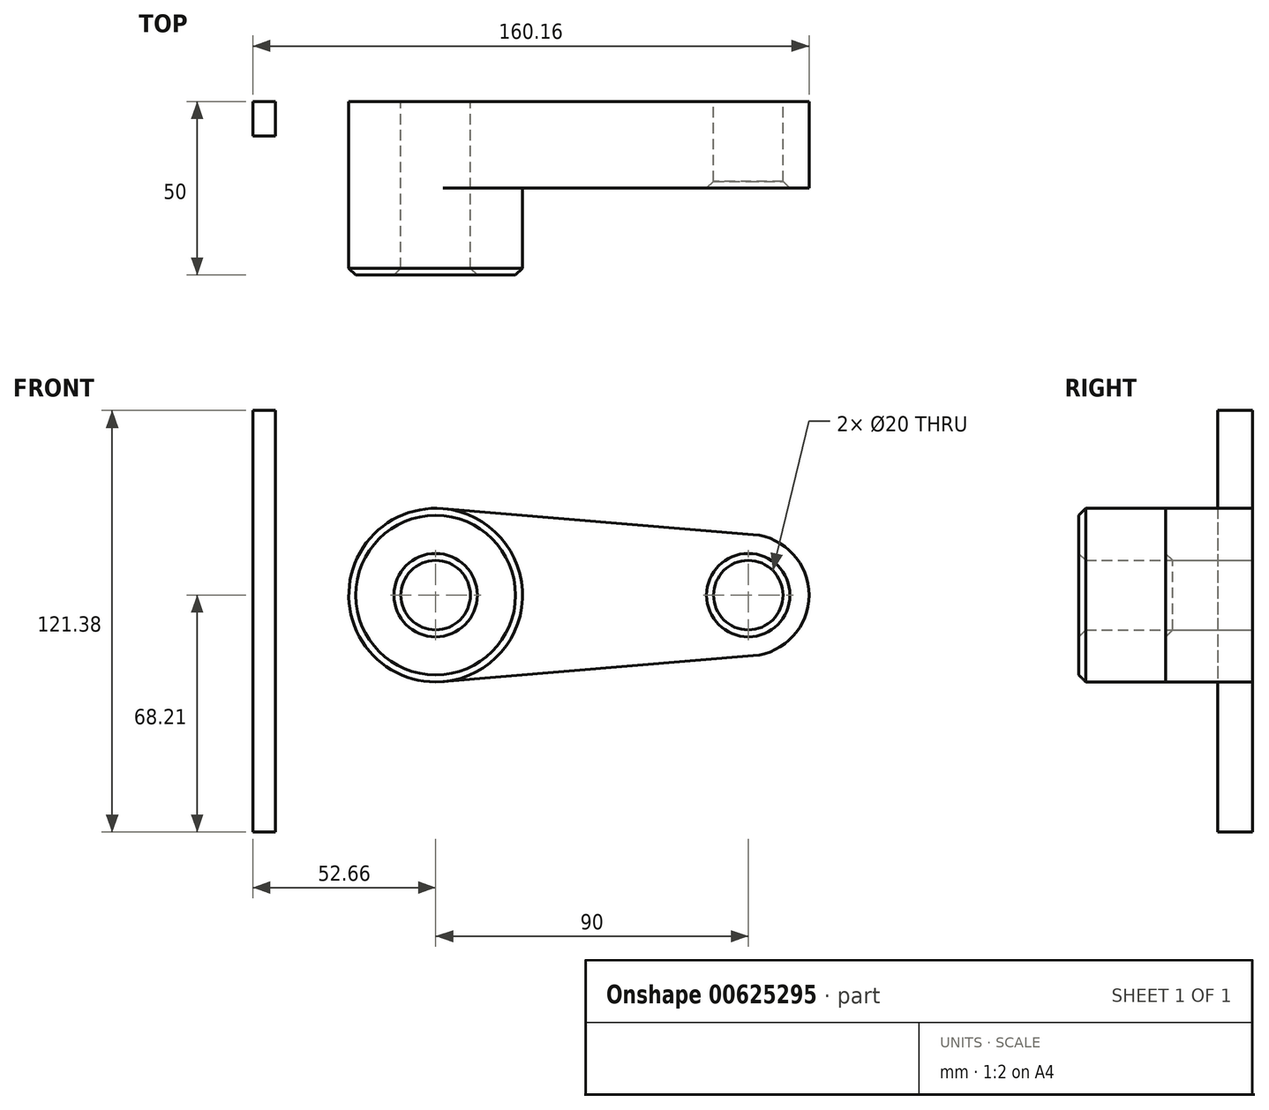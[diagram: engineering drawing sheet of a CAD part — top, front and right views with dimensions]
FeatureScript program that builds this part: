
annotation { "Feature Type Name" : "Feature", "Feature Type Description" : "" }
export const myFeature = defineFeature(function(context is Context, id is Id, definition is map)
    precondition{}
    {
        {
            var Q0;
            Q0=qCreatedBy(makeId("Front.planeOp"),FACE);
            var sketch = newSketch(context, id + "F0", { "sketchPlane" : qUnion([Q0])});
            skCircle(sketch, "E0", {"center": v(0, 0) * mm, "radius": 25 * mm});
            skCircle(sketch, "E1", {"center": v(90, 0) * mm, "radius": 17.5 * mm});
            skLineSegment(sketch, "E2", {"start": v(2.08, 24.91) * mm, "end": v(91.46, 17.44) * mm});
            skLineSegment(sketch, "E3", {"start": v(2.08, -24.91) * mm, "end": v(91.46, -17.44) * mm});
            skCircle(sketch, "E4", {"center": v(0, 0) * mm, "radius": 10 * mm});
            skCircle(sketch, "E5", {"center": v(90, 0) * mm, "radius": 10 * mm});
            skSolve(sketch);
        }
        {
            var Q0;
            Q0=qSketchRegion(id+"F0",true);
            extrude(context, id + "F1", {"entities" : qUnion([Q0]), "depth" : 25 * mm});
        }
        {
            var Q0;
            Q0=makeQuery(id+"F0.imprint","IMPRINT",FACE,{"disambiguationData":[TD([[makeQuery(id+"F0.imprint","IMPRINT",EDGE,{"derivedFrom":sQuery(id+"F0.wireOp",EDGE,"E4")}),-1.0]])]});
            extrude(context, id + "F2", {"entities" : qUnion([Q0]), "operationType" : NewBodyOperationType.ADD, "depth" : 50 * mm});
        }
        {
            var Q0;
            Q0=makeQuery(id+"F2.opExtrude","CAP_EDGE",EDGE,{"disambiguationData":[OSD([sQuery(id+"F0.wireOp",EDGE,"E0")])],"isStart":false});
            var Q1;
            Q1=makeQuery(id+"F2.opExtrude","CAP_EDGE",EDGE,{"disambiguationData":[OSD([sQuery(id+"F0.wireOp",EDGE,"E4")])],"isStart":false});
            var Q2;
            Q2=makeQuery(id+"F1.opExtrude","CAP_EDGE",EDGE,{"disambiguationData":[OSD([sQuery(id+"F0.wireOp",EDGE,"E5")])],"isStart":false});
            chamfer(context, id + "F3", {"entities" : qUnion([Q0, Q1, Q2]), "width" : 2 * mm, "tangentPropagation" : true});
        }
        {
            var Q0;
            Q0=qCreatedBy(makeId("Front.planeOp"),FACE);
            var sketch = newSketch(context, id + "F4", { "sketchPlane" : qUnion([Q0])});
            skLineSegment(sketch, "E6.bottom", {"start": v(-52.66, 53.17) * mm, "end": v(-46.1, 53.17) * mm});
            skLineSegment(sketch, "E6.top", {"start": v(-52.66, -68.2) * mm, "end": v(-46.1, -68.2) * mm});
            skLineSegment(sketch, "E6.left", {"start": v(-52.66, 53.17) * mm, "end": v(-52.66, -68.2) * mm});
            skLineSegment(sketch, "E6.right", {"start": v(-46.1, 53.17) * mm, "end": v(-46.1, -68.2) * mm});
            skSolve(sketch);
        }
        {
            var Q0;
            Q0=makeQuery(id+"F4.imprint","IMPRINT",FACE,{"disambiguationData":[TD([[makeQuery(id+"F4.imprint","IMPRINT",EDGE,{"derivedFrom":sQuery(id+"F4.wireOp",EDGE,"E6.bottom")}),-1.0]])]});
            extrude(context, id + "F5", {"entities" : qUnion([Q0]), "depth" : 10 * mm, "offsetDistance" : 25 * mm});
        }
    });
